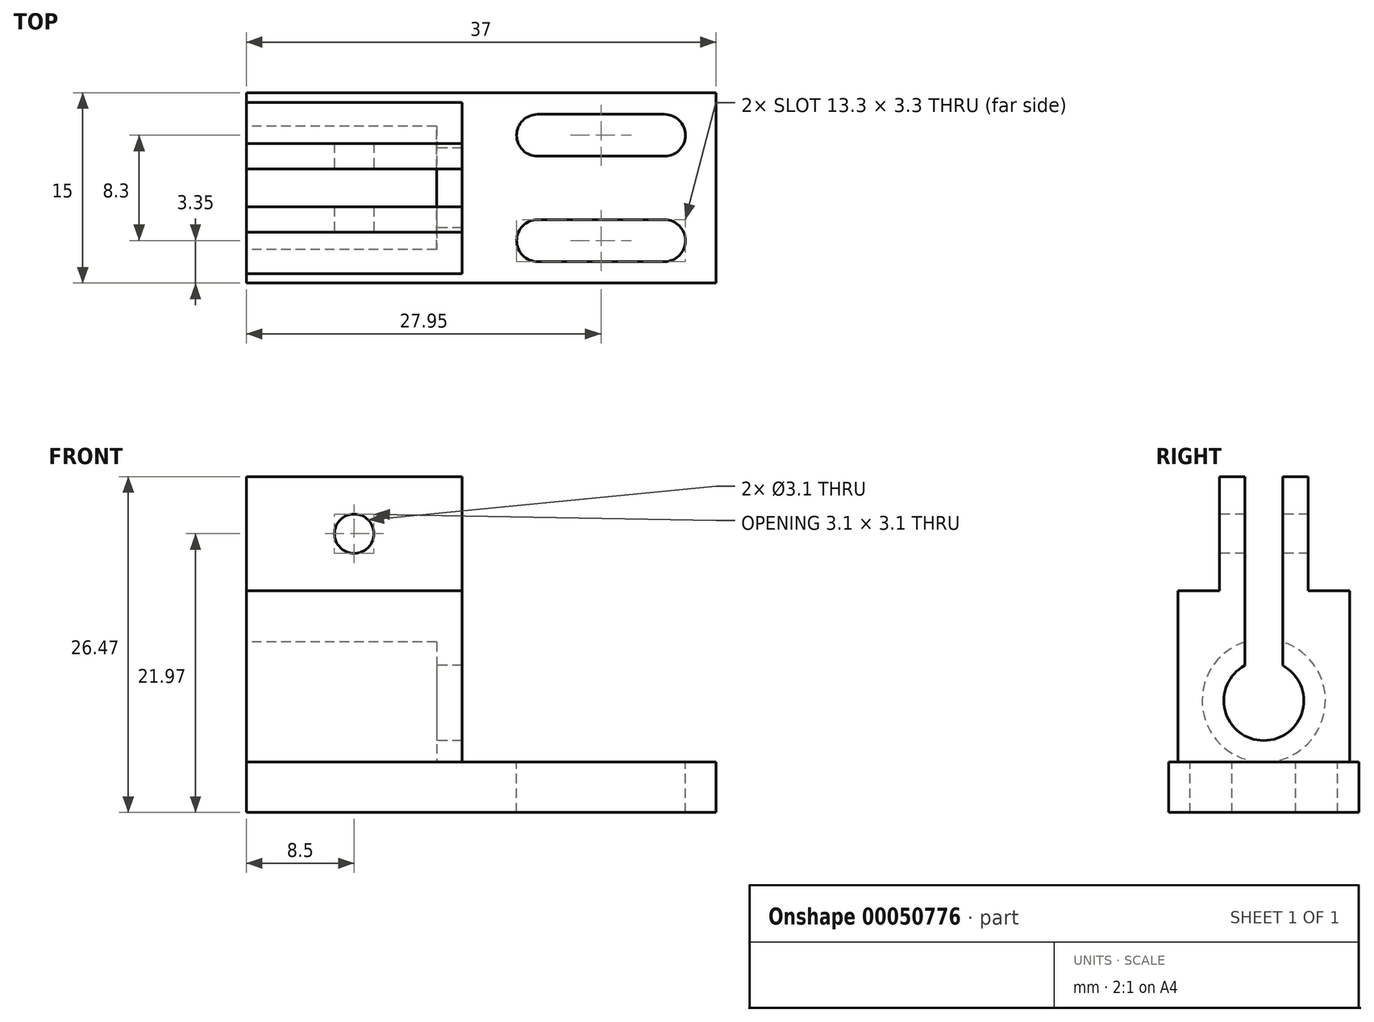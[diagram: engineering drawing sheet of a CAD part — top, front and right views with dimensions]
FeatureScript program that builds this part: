
annotation { "Feature Type Name" : "Feature", "Feature Type Description" : "" }
export const myFeature = defineFeature(function(context is Context, id is Id, definition is map)
    precondition{}
    {
        {
            var Q0;
            Q0=qCreatedBy(makeId("Top.planeOp"),FACE);
            var sketch = newSketch(context, id + "F0", { "sketchPlane" : qUnion([Q0])});
            skLineSegment(sketch, "E0.bottom", {"start": v(-18.5, 7.5) * mm, "end": v(18.5, 7.5) * mm});
            skLineSegment(sketch, "E0.top", {"start": v(-18.5, -7.5) * mm, "end": v(18.5, -7.5) * mm});
            skLineSegment(sketch, "E0.left", {"start": v(-18.5, 7.5) * mm, "end": v(-18.5, -7.5) * mm});
            skLineSegment(sketch, "E0.right", {"start": v(18.5, 7.5) * mm, "end": v(18.5, -7.5) * mm});
            skSolve(sketch);
        }
        {
            var Q0;
            Q0 = qSketchRegion(id + "F0", true);
            extrude(context, id + "F1", {"entities" : qUnion([Q0]), "depth" : 3.97 * mm});
        }
        {
            var Q0;
            Q0=makeQuery(id+"F1.opExtrude","CAP_FACE",FACE,{"disambiguationData":[OSD([sQuery(id+"F0.wireOp",EDGE,"E0.bottom"),sQuery(id+"F0.wireOp",EDGE,"E0.top"),sQuery(id+"F0.wireOp",EDGE,"E0.left"),sQuery(id+"F0.wireOp",EDGE,"E0.right")])],"isStart":false});
            var sketch = newSketch(context, id + "F2", { "sketchPlane" : qUnion([Q0])});
            skLineSegment(sketch, "E1.bottom", {"start": v(-18.5, 6.75) * mm, "end": v(-1.5, 6.75) * mm});
            skLineSegment(sketch, "E1.top", {"start": v(-18.5, -6.75) * mm, "end": v(-1.5, -6.75) * mm});
            skLineSegment(sketch, "E1.left", {"start": v(-18.5, 6.75) * mm, "end": v(-18.5, -6.75) * mm});
            skLineSegment(sketch, "E1.right", {"start": v(-1.5, 6.75) * mm, "end": v(-1.5, -6.75) * mm});
            skSolve(sketch);
        }
        {
            var Q0;
            Q0 = qSketchRegion(id + "F2", true);
            extrude(context, id + "F3", {"entities" : qUnion([Q0]), "operationType" : NewBodyOperationType.ADD, "depth" : 13.5 * mm});
        }
        {
            var Q0;
            Q0=makeQuery(id+"F3.boolean.opBoolean","MERGE",FACE,{"derivedFrom":[makeQuery(id+"F1.opExtrude","SWEPT_FACE",FACE,{"disambiguationData":[OSD([sQuery(id+"F0.wireOp",EDGE,"E0.left")])]}),makeQuery(id+"F3.opExtrude","SWEPT_FACE",FACE,{"disambiguationData":[OSD([sQuery(id+"F2.wireOp",EDGE,"E1.left")])]})]});
            var sketch = newSketch(context, id + "F4", { "sketchPlane" : qUnion([Q0])});
            skCircle(sketch, "E2", {"center": v(0, 8.82) * mm, "radius": 4.85 * mm});
            skSolve(sketch);
        }
        {
            var Q0;
            Q0 = qSketchRegion(id + "F4", true);
            extrude(context, id + "F5", {"entities" : qUnion([Q0]), "operationType" : NewBodyOperationType.REMOVE, "oppositeDirection" : true, "depth" : 15 * mm});
        }
        {
            var Q0;
            Q0=makeQuery(id+"F5.boolean.opBoolean","COPY",FACE,{"derivedFrom":makeQuery(id+"F5.opExtrude","CAP_FACE",FACE,{"disambiguationData":[OSD([sQuery(id+"F4.wireOp",EDGE,"E2")])],"isStart":false})});
            var sketch = newSketch(context, id + "F6", { "sketchPlane" : qUnion([Q0])});
            skCircle(sketch, "E3", {"center": v(0, 8.82) * mm, "radius": 3.15 * mm});
            skSolve(sketch);
        }
        {
            var Q0;
            Q0 = qSketchRegion(id + "F6", true);
            extrude(context, id + "F7", {"entities" : qUnion([Q0]), "operationType" : NewBodyOperationType.REMOVE, "endBound" : BoundingType.THROUGH_ALL, "oppositeDirection" : true, "depth" : 25 * mm});
        }
        {
            var Q0;
            Q0=makeQuery(id+"F3.opExtrude","CAP_FACE",FACE,{"disambiguationData":[OSD([sQuery(id+"F2.wireOp",EDGE,"E1.bottom"),sQuery(id+"F2.wireOp",EDGE,"E1.top"),sQuery(id+"F2.wireOp",EDGE,"E1.left"),sQuery(id+"F2.wireOp",EDGE,"E1.right")])],"isStart":false});
            var sketch = newSketch(context, id + "F8", { "sketchPlane" : qUnion([Q0])});
            skLineSegment(sketch, "E4.bottom", {"start": v(-1.5, 3.5) * mm, "end": v(-18.5, 3.5) * mm});
            skLineSegment(sketch, "E4.top", {"start": v(-1.5, -3.5) * mm, "end": v(-18.5, -3.5) * mm});
            skLineSegment(sketch, "E4.left", {"start": v(-1.5, 3.5) * mm, "end": v(-1.5, -3.5) * mm});
            skLineSegment(sketch, "E4.right", {"start": v(-18.5, 3.5) * mm, "end": v(-18.5, -3.5) * mm});
            skSolve(sketch);
        }
        {
            var Q0;
            Q0 = qSketchRegion(id + "F8", true);
            extrude(context, id + "F9", {"entities" : qUnion([Q0]), "operationType" : NewBodyOperationType.ADD, "depth" : 9 * mm});
        }
        {
            var Q0;
            Q0=makeQuery(id+"F9.opExtrude","SWEPT_FACE",FACE,{"disambiguationData":[OSD([sQuery(id+"F8.wireOp",EDGE,"E4.top")])]});
            var sketch = newSketch(context, id + "F10", { "sketchPlane" : qUnion([Q0])});
            skCircle(sketch, "E5", {"center": v(-10, 21.97) * mm, "radius": 1.55 * mm});
            skSolve(sketch);
        }
        {
            var Q0;
            Q0 = qSketchRegion(id + "F10", true);
            extrude(context, id + "F11", {"entities" : qUnion([Q0]), "operationType" : NewBodyOperationType.REMOVE, "endBound" : BoundingType.THROUGH_ALL, "oppositeDirection" : true, "depth" : 25 * mm});
        }
        {
            var Q0;
            Q0=makeQuery(id+"F9.opExtrude","CAP_FACE",FACE,{"disambiguationData":[OSD([sQuery(id+"F8.wireOp",EDGE,"E4.bottom"),sQuery(id+"F8.wireOp",EDGE,"E4.top"),sQuery(id+"F8.wireOp",EDGE,"E4.left"),sQuery(id+"F8.wireOp",EDGE,"E4.right")])],"isStart":false});
            var sketch = newSketch(context, id + "F12", { "sketchPlane" : qUnion([Q0])});
            skLineSegment(sketch, "E6.bottom", {"start": v(-1.5, 1.5) * mm, "end": v(-18.5, 1.5) * mm});
            skLineSegment(sketch, "E6.top", {"start": v(-1.5, -1.5) * mm, "end": v(-18.5, -1.5) * mm});
            skLineSegment(sketch, "E6.left", {"start": v(-1.5, 1.5) * mm, "end": v(-1.5, -1.5) * mm});
            skLineSegment(sketch, "E6.right", {"start": v(-18.5, 1.5) * mm, "end": v(-18.5, -1.5) * mm});
            skSolve(sketch);
        }
        {
            var Q0;
            Q0 = qSketchRegion(id + "F12", true);
            extrude(context, id + "F13", {"entities" : qUnion([Q0]), "operationType" : NewBodyOperationType.REMOVE, "oppositeDirection" : true, "depth" : 17.5 * mm});
        }
        {
            var Q0;
            Q0=makeQuery(id+"F1.opExtrude","CAP_FACE",FACE,{"disambiguationData":[OSD([sQuery(id+"F0.wireOp",EDGE,"E0.bottom"),sQuery(id+"F0.wireOp",EDGE,"E0.top"),sQuery(id+"F0.wireOp",EDGE,"E0.left"),sQuery(id+"F0.wireOp",EDGE,"E0.right")])],"isStart":false});
            var sketch = newSketch(context, id + "F14", { "sketchPlane" : qUnion([Q0])});
            skLineSegment(sketch, "E7.bottom", {"start": v(4.45, 5.8) * mm, "end": v(14.45, 5.8) * mm});
            skLineSegment(sketch, "E7.top", {"start": v(4.45, 2.5) * mm, "end": v(14.45, 2.5) * mm});
            skLineSegment(sketch, "E8.bottom", {"start": v(4.45, -2.5) * mm, "end": v(14.45, -2.5) * mm});
            skLineSegment(sketch, "E8.top", {"start": v(4.45, -5.8) * mm, "end": v(14.45, -5.8) * mm});
            skArc(sketch, "E9", {"start": v(14.45, 2.5) * mm, "mid": v(16.1, 4.15) * mm, "end": v(14.45, 5.8) * mm});
            skArc(sketch, "E10", {"start": v(4.45, 5.8) * mm, "mid": v(2.8, 4.15) * mm, "end": v(4.45, 2.5) * mm});
            skArc(sketch, "E11", {"start": v(14.45, -5.8) * mm, "mid": v(16.1, -4.15) * mm, "end": v(14.45, -2.5) * mm});
            skArc(sketch, "E12", {"start": v(4.45, -2.5) * mm, "mid": v(2.8, -4.15) * mm, "end": v(4.45, -5.8) * mm});
            skSolve(sketch);
        }
        {
            var Q0;
            Q0 = qSketchRegion(id + "F14", true);
            extrude(context, id + "F15", {"entities" : qUnion([Q0]), "operationType" : NewBodyOperationType.REMOVE, "endBound" : BoundingType.THROUGH_ALL, "oppositeDirection" : true, "depth" : 25 * mm});
        }
    });
